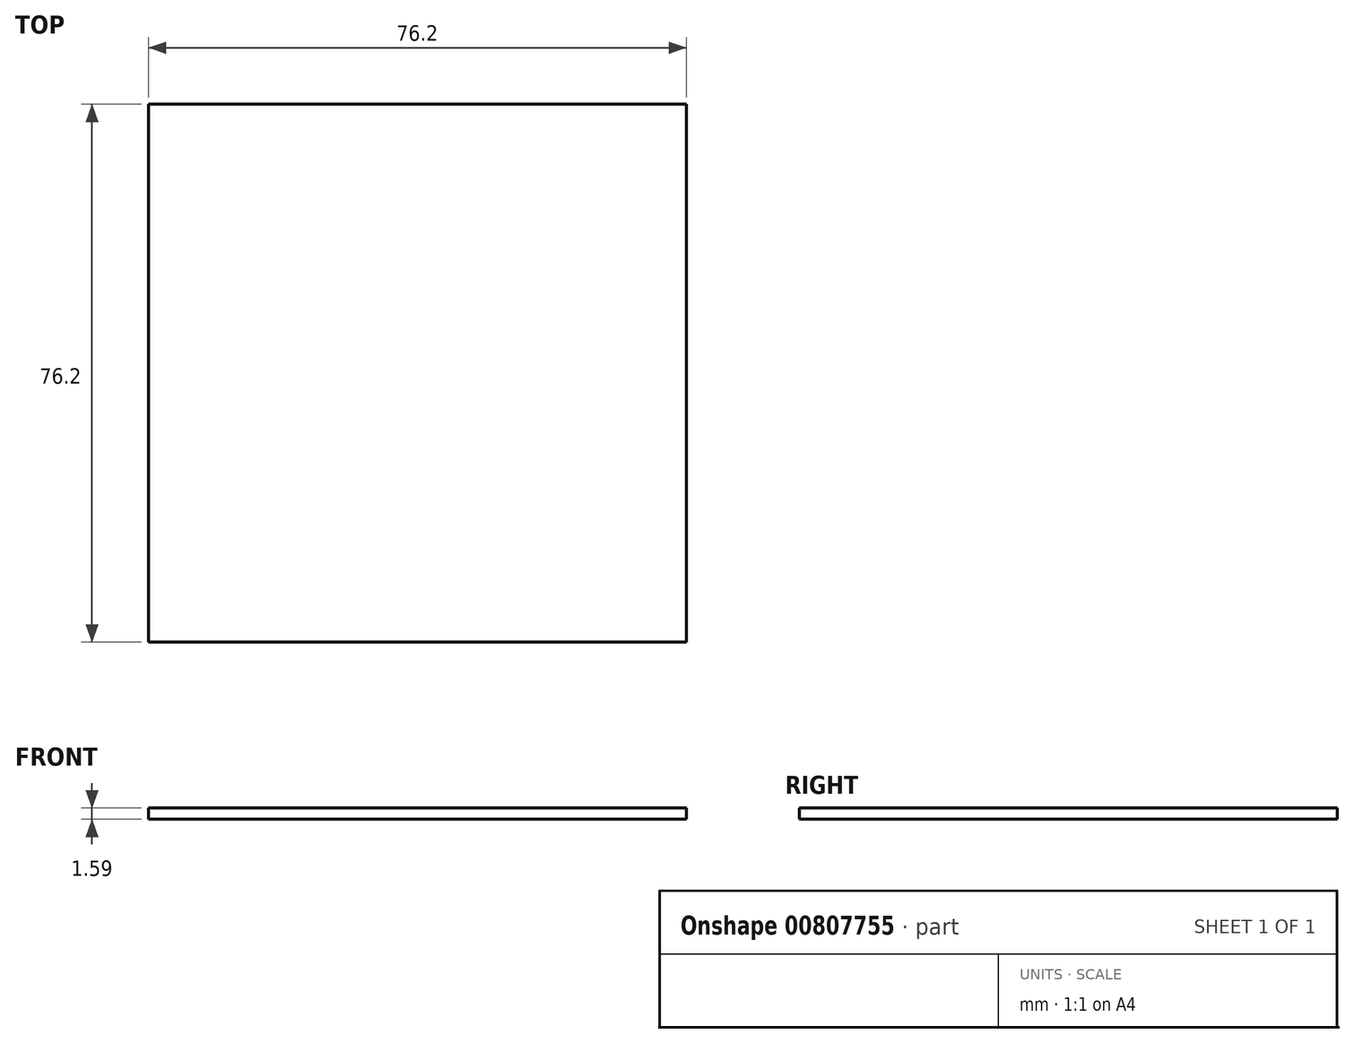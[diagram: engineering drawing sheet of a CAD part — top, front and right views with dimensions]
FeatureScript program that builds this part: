
annotation { "Feature Type Name" : "Feature", "Feature Type Description" : "" }
export const myFeature = defineFeature(function(context is Context, id is Id, definition is map)
    precondition{}
    {
        {
            var Q0;
            Q0=qCreatedBy(makeId("Top.planeOp"),FACE);
            var sketch = newSketch(context, id + "F0", { "sketchPlane" : qUnion([Q0])});
            skLineSegment(sketch, "E0.bottom", {"start": v(-38.1, 38.1) * mm, "end": v(38.1, 38.1) * mm});
            skLineSegment(sketch, "E0.top", {"start": v(-38.1, -38.1) * mm, "end": v(38.1, -38.1) * mm});
            skLineSegment(sketch, "E0.left", {"start": v(-38.1, 38.1) * mm, "end": v(-38.1, -38.1) * mm});
            skLineSegment(sketch, "E0.right", {"start": v(38.1, 38.1) * mm, "end": v(38.1, -38.1) * mm});
            skPoint(sketch, "E0.middle", {"position": v(0, 0) * mm});
            skSolve(sketch);
        }
        {
            var Q0;
            Q0 = qSketchRegion(id + "F0", true);
            extrude(context, id + "F1", {"entities" : qUnion([Q0]), "depth" : 1.59 * mm, "offsetDistance" : 25.4 * mm});
        }
    });
